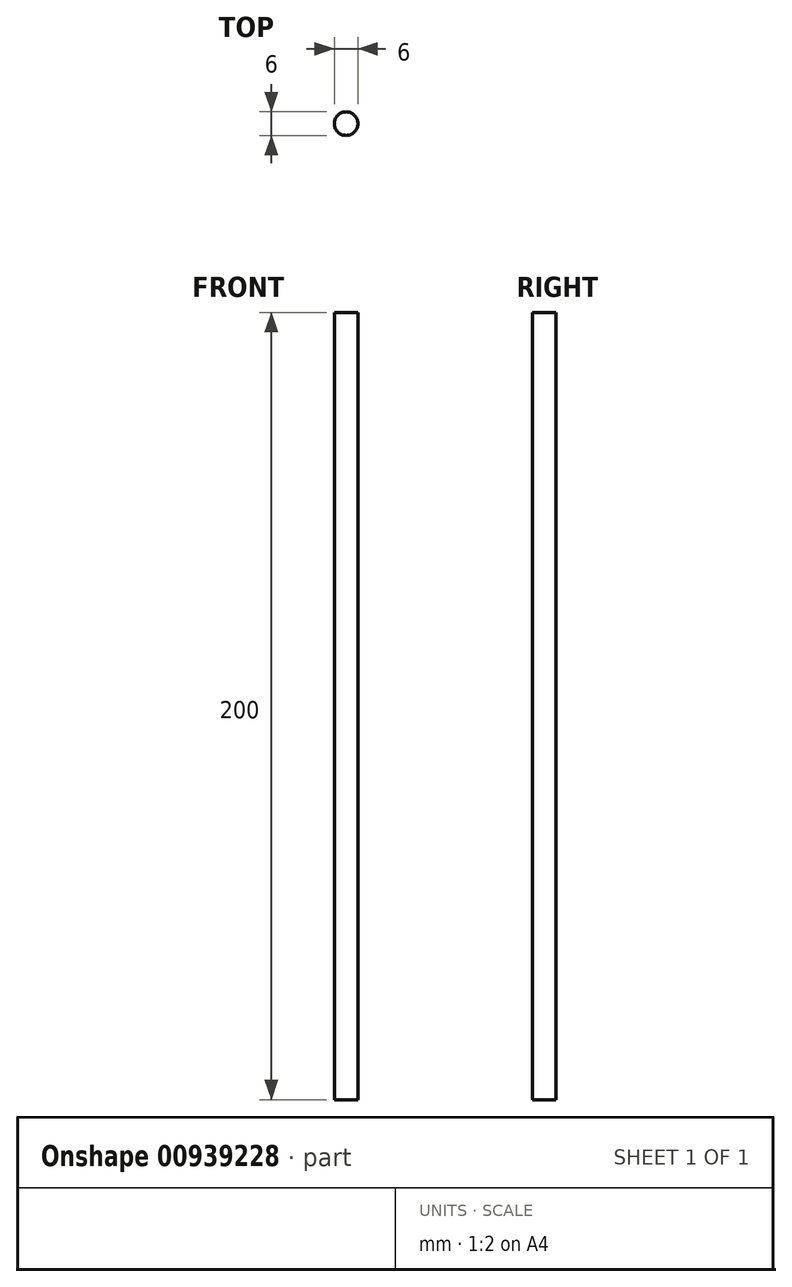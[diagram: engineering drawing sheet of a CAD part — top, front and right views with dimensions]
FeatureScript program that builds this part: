
annotation { "Feature Type Name" : "Feature", "Feature Type Description" : "" }
export const myFeature = defineFeature(function(context is Context, id is Id, definition is map)
    precondition{}
    {
        {
            var Q0;
            Q0=qCreatedBy(makeId("Top.planeOp"),FACE);
            var sketch = newSketch(context, id + "F0", { "sketchPlane" : qUnion([Q0])});
            skCircle(sketch, "E0", {"center": v(0, 0) * mm, "radius": 3 * mm});
            skSolve(sketch);
        }
        {
            var Q0;
            Q0=makeQuery(id+"F0.imprint","IMPRINT",FACE,{"disambiguationData":[TD([[makeQuery(id+"F0.imprint","IMPRINT",EDGE,{"derivedFrom":sQuery(id+"F0.wireOp",EDGE,"E0")}),1.0]])]});
            extrude(context, id + "F1", {"entities" : qUnion([Q0]), "depth" : 200 * mm, "offsetDistance" : 25 * mm});
        }
    });
